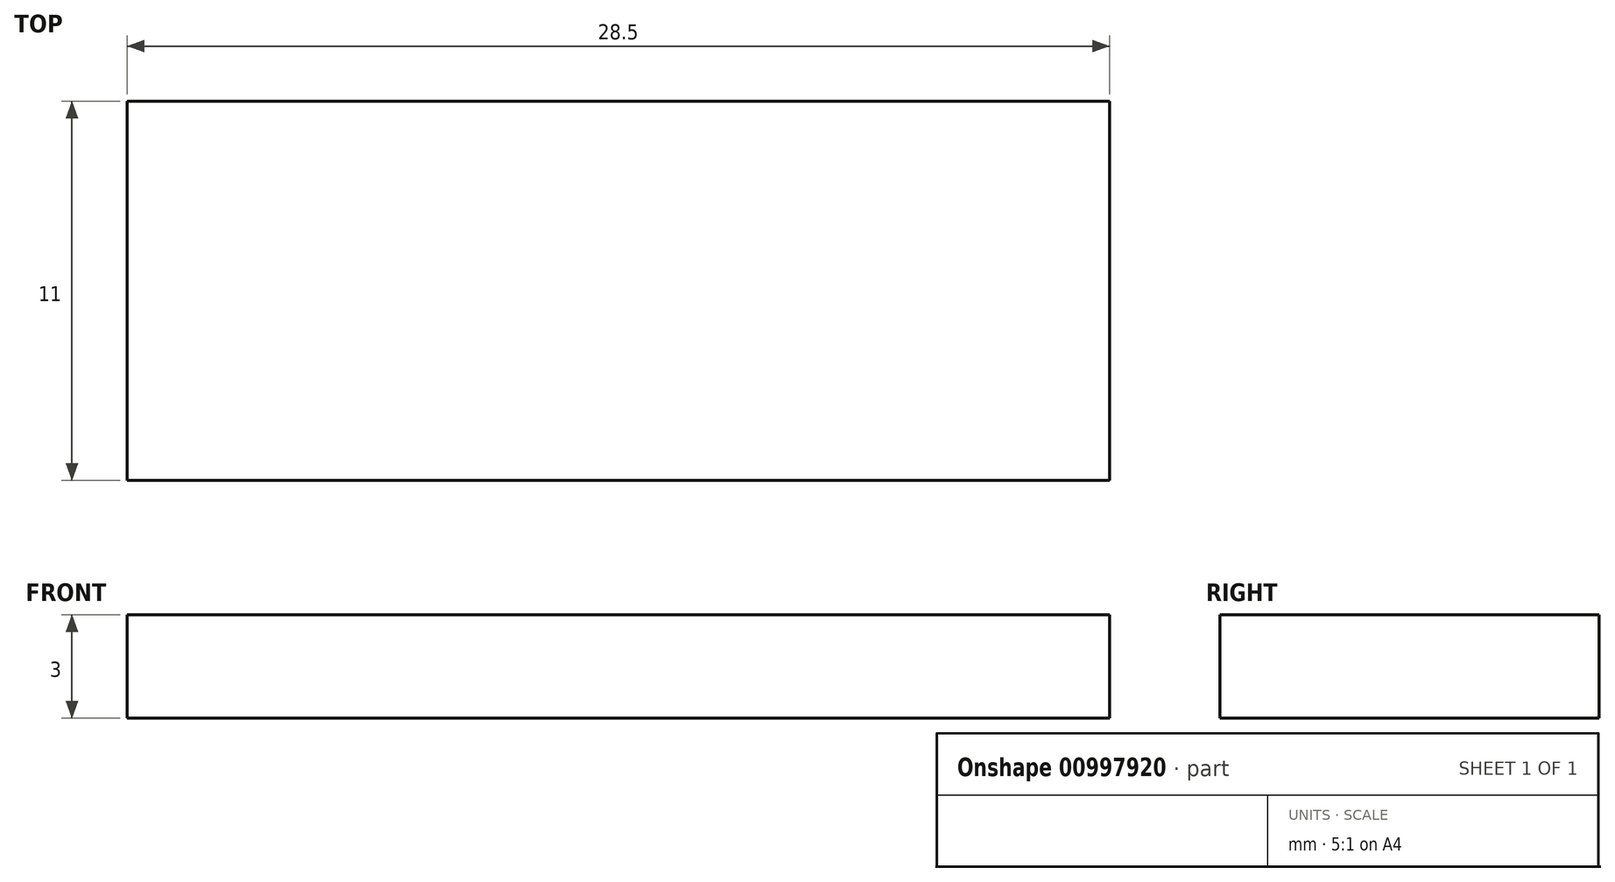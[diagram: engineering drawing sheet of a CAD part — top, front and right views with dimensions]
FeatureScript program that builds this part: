
annotation { "Feature Type Name" : "Feature", "Feature Type Description" : "" }
export const myFeature = defineFeature(function(context is Context, id is Id, definition is map)
    precondition{}
    {
        {
            var Q0;
            Q0=qCreatedBy(makeId("Front.planeOp"),FACE);
            var sketch = newSketch(context, id + "F0", { "sketchPlane" : qUnion([Q0])});
            skLineSegment(sketch, "E0.bottom", {"start": v(14.25, -1.5) * mm, "end": v(-14.25, -1.5) * mm});
            skLineSegment(sketch, "E0.top", {"start": v(14.25, 1.5) * mm, "end": v(-14.25, 1.5) * mm});
            skLineSegment(sketch, "E0.left", {"start": v(14.25, -1.5) * mm, "end": v(14.25, 1.5) * mm});
            skLineSegment(sketch, "E0.right", {"start": v(-14.25, -1.5) * mm, "end": v(-14.25, 1.5) * mm});
            skPoint(sketch, "E0.middle", {"position": v(0, 0) * mm});
            skSolve(sketch);
        }
        {
            var Q0;
            Q0=makeQuery(id+"F0.imprint","IMPRINT",FACE,{"disambiguationData":[TD([[makeQuery(id+"F0.imprint","IMPRINT",EDGE,{"derivedFrom":sQuery(id+"F0.wireOp",EDGE,"E0.bottom")}),-1.0]])]});
            extrude(context, id + "F1", {"entities" : qUnion([Q0]), "depth" : 11 * mm, "offsetDistance" : 25 * mm});
        }
    });
